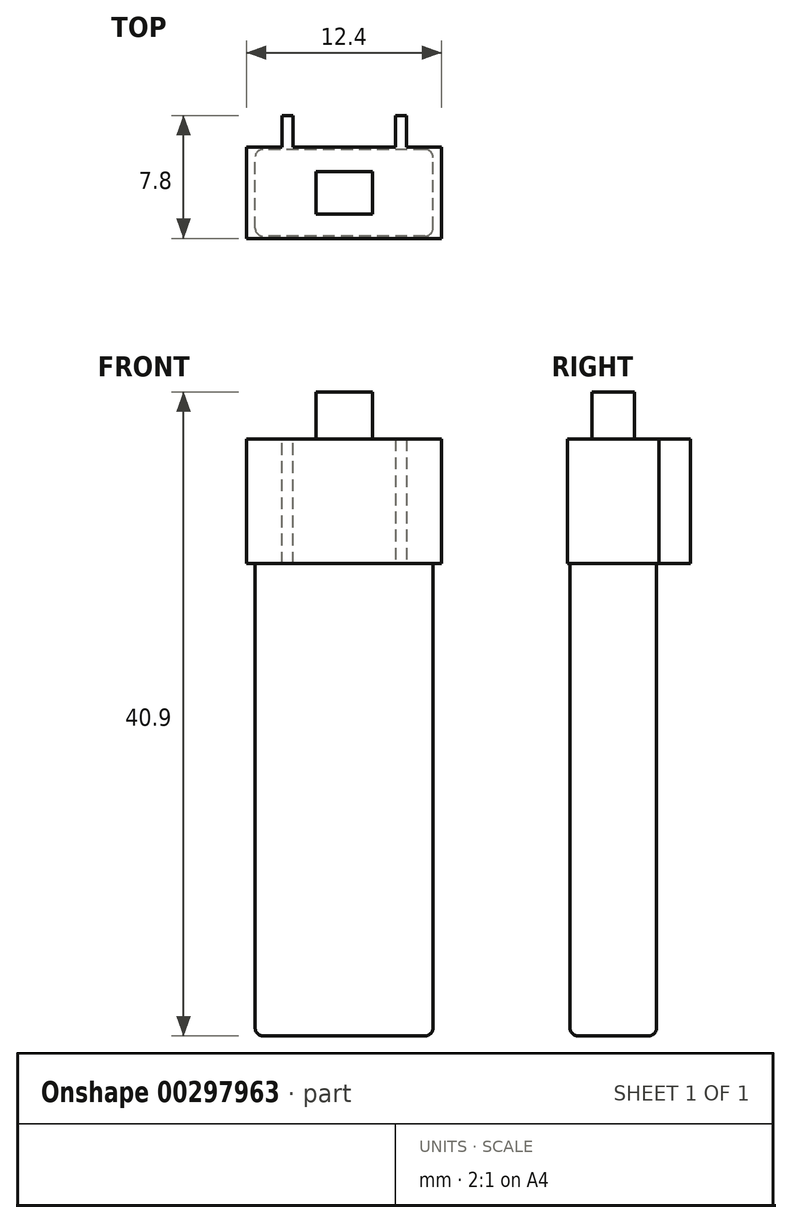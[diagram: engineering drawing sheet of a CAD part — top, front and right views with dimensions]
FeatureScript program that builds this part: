
annotation { "Feature Type Name" : "Feature", "Feature Type Description" : "" }
export const myFeature = defineFeature(function(context is Context, id is Id, definition is map)
    precondition{}
    {
        {
            var Q0;
            Q0=qCreatedBy(makeId("Top.planeOp"),FACE);
            var sketch = newSketch(context, id + "F0", { "sketchPlane" : qUnion([Q0])});
            skLineSegment(sketch, "E0.bottom", {"start": v(6.2, 2.9) * mm, "end": v(-6.2, 2.9) * mm});
            skLineSegment(sketch, "E0.top", {"start": v(6.2, -2.9) * mm, "end": v(-6.2, -2.9) * mm});
            skLineSegment(sketch, "E0.left", {"start": v(6.2, 2.9) * mm, "end": v(6.2, -2.9) * mm});
            skLineSegment(sketch, "E0.right", {"start": v(-6.2, 2.9) * mm, "end": v(-6.2, -2.9) * mm});
            skPoint(sketch, "E0.middle", {"position": v(0, 0) * mm});
            skSolve(sketch);
        }
        {
            var Q0;
            Q0 = qSketchRegion(id + "F0", true);
            extrude(context, id + "F1", {"entities" : qUnion([Q0]), "depth" : 7.9 * mm});
        }
        {
            var Q0;
            Q0=makeQuery(id+"F1.opExtrude","CAP_FACE",FACE,{"disambiguationData":[OSD([sQuery(id+"F0.wireOp",EDGE,"E0.bottom"),sQuery(id+"F0.wireOp",EDGE,"E0.top"),sQuery(id+"F0.wireOp",EDGE,"E0.left"),sQuery(id+"F0.wireOp",EDGE,"E0.right")])],"isStart":true});
            var sketch = newSketch(context, id + "F2", { "sketchPlane" : qUnion([Q0])});
            skLineSegment(sketch, "E1.bottom", {"start": v(5.65, 2.75) * mm, "end": v(-5.65, 2.75) * mm});
            skLineSegment(sketch, "E1.top", {"start": v(5.65, -2.75) * mm, "end": v(-5.65, -2.75) * mm});
            skLineSegment(sketch, "E1.left", {"start": v(5.65, 2.75) * mm, "end": v(5.65, -2.75) * mm});
            skLineSegment(sketch, "E1.right", {"start": v(-5.65, 2.75) * mm, "end": v(-5.65, -2.75) * mm});
            skPoint(sketch, "E1.middle", {"position": v(0, 0) * mm});
            skSolve(sketch);
        }
        {
            var Q0;
            Q0=makeQuery(id+"F2.imprint","IMPRINT",FACE,{"disambiguationData":[TD([[makeQuery(id+"F2.imprint","IMPRINT",EDGE,{"derivedFrom":sQuery(id+"F2.wireOp",EDGE,"E1.bottom")}),1.0]])]});
            extrude(context, id + "F3", {"entities" : qUnion([Q0]), "operationType" : NewBodyOperationType.ADD, "depth" : 30 * mm});
        }
        {
            var Q0;
            Q0=makeQuery(id+"F3.opExtrude","SWEPT_EDGE",EDGE,{"disambiguationData":[OSD([sQuery(id+"F2.wireOp",EDGE,"E1.bottom"),sQuery(id+"F2.wireOp",EDGE,"E1.right")])]});
            var Q1;
            Q1=makeQuery(id+"F3.opExtrude","SWEPT_EDGE",EDGE,{"disambiguationData":[OSD([sQuery(id+"F2.wireOp",EDGE,"E1.bottom"),sQuery(id+"F2.wireOp",EDGE,"E1.left")])]});
            var Q2;
            Q2=makeQuery(id+"F3.opExtrude","CAP_EDGE",EDGE,{"disambiguationData":[OSD([sQuery(id+"F2.wireOp",EDGE,"E1.bottom")])],"isStart":false});
            var Q3;
            Q3=makeQuery(id+"F3.opExtrude","CAP_EDGE",EDGE,{"disambiguationData":[OSD([sQuery(id+"F2.wireOp",EDGE,"E1.left")])],"isStart":false});
            var Q4;
            Q4=makeQuery(id+"F3.opExtrude","CAP_EDGE",EDGE,{"disambiguationData":[OSD([sQuery(id+"F2.wireOp",EDGE,"E1.top")])],"isStart":false});
            var Q5;
            Q5=makeQuery(id+"F3.opExtrude","CAP_EDGE",EDGE,{"disambiguationData":[OSD([sQuery(id+"F2.wireOp",EDGE,"E1.right")])],"isStart":false});
            var Q6;
            Q6=makeQuery(id+"F3.opExtrude","SWEPT_EDGE",EDGE,{"disambiguationData":[OSD([sQuery(id+"F2.wireOp",EDGE,"E1.top"),sQuery(id+"F2.wireOp",EDGE,"E1.left")])]});
            var Q7;
            Q7=makeQuery(id+"F3.opExtrude","SWEPT_EDGE",EDGE,{"disambiguationData":[OSD([sQuery(id+"F2.wireOp",EDGE,"E1.top"),sQuery(id+"F2.wireOp",EDGE,"E1.right")])]});
            fillet(context, id + "F4", {"entities" : qUnion([Q0, Q1, Q2, Q3, Q4, Q5, Q6, Q7]), "radius" : .5 * mm, "tangentPropagation" : true, "allowEdgeOverflow" : false});
        }
        {
            var Q0;
            Q0=makeQuery(id+"F1.opExtrude","CAP_FACE",FACE,{"disambiguationData":[OSD([sQuery(id+"F0.wireOp",EDGE,"E0.bottom"),sQuery(id+"F0.wireOp",EDGE,"E0.top"),sQuery(id+"F0.wireOp",EDGE,"E0.left"),sQuery(id+"F0.wireOp",EDGE,"E0.right")])],"isStart":false});
            var sketch = newSketch(context, id + "F5", { "sketchPlane" : qUnion([Q0])});
            skLineSegment(sketch, "E2.bottom", {"start": v(1.8, 1.35) * mm, "end": v(-1.8, 1.35) * mm});
            skLineSegment(sketch, "E2.top", {"start": v(1.8, -1.35) * mm, "end": v(-1.8, -1.35) * mm});
            skLineSegment(sketch, "E2.left", {"start": v(1.8, 1.35) * mm, "end": v(1.8, -1.35) * mm});
            skLineSegment(sketch, "E2.right", {"start": v(-1.8, 1.35) * mm, "end": v(-1.8, -1.35) * mm});
            skPoint(sketch, "E2.middle", {"position": v(0, 0) * mm});
            skSolve(sketch);
        }
        {
            var Q0;
            Q0=makeQuery(id+"F5.imprint","IMPRINT",FACE,{"disambiguationData":[TD([[makeQuery(id+"F5.imprint","IMPRINT",EDGE,{"derivedFrom":sQuery(id+"F5.wireOp",EDGE,"E2.bottom")}),1.0]])]});
            extrude(context, id + "F6", {"entities" : qUnion([Q0]), "operationType" : NewBodyOperationType.ADD, "depth" : 3 * mm});
        }
        {
            var Q0;
            Q0=makeQuery(id+"F1.opExtrude","SWEPT_FACE",FACE,{"disambiguationData":[OSD([sQuery(id+"F0.wireOp",EDGE,"E0.bottom")])]});
            var sketch = newSketch(context, id + "F7", { "sketchPlane" : qUnion([Q0])});
            skLineSegment(sketch, "E3.bottom", {"start": v(3.95, 0) * mm, "end": v(3.25, 0) * mm});
            skLineSegment(sketch, "E3.top", {"start": v(3.95, 7.9) * mm, "end": v(3.25, 7.9) * mm});
            skLineSegment(sketch, "E3.left", {"start": v(3.95, 0) * mm, "end": v(3.95, 7.9) * mm});
            skLineSegment(sketch, "E3.right", {"start": v(3.25, 0) * mm, "end": v(3.25, 7.9) * mm});
            skLineSegment(sketch, "E4.bottom", {"start": v(-3.25, 7.9) * mm, "end": v(-3.95, 7.9) * mm});
            skLineSegment(sketch, "E4.top", {"start": v(-3.25, 0) * mm, "end": v(-3.95, 0) * mm});
            skLineSegment(sketch, "E4.left", {"start": v(-3.25, 7.9) * mm, "end": v(-3.25, 0) * mm});
            skLineSegment(sketch, "E4.right", {"start": v(-3.95, 7.9) * mm, "end": v(-3.95, 0) * mm});
            skSolve(sketch);
        }
        {
            var Q0;
            Q0=makeQuery(id+"F7.imprint","IMPRINT",FACE,{"disambiguationData":[TD([[makeQuery(id+"F7.imprint","IMPRINT",EDGE,{"derivedFrom":sQuery(id+"F7.wireOp",EDGE,"E3.bottom")}),1.0]])]});
            var Q1;
            Q1=makeQuery(id+"F7.imprint","IMPRINT",FACE,{"disambiguationData":[TD([[makeQuery(id+"F7.imprint","IMPRINT",EDGE,{"derivedFrom":sQuery(id+"F7.wireOp",EDGE,"E4.bottom")}),-1.0]])]});
            extrude(context, id + "F8", {"entities" : qUnion([Q0, Q1]), "operationType" : NewBodyOperationType.ADD, "depth" : 2 * mm});
        }
    });
